# Revit family: Hager-Golf-IP40-Plain_Door-sistema-PT-pt
name_source: partatom
category: Electrical Equipment
units: mm (PartAtom-declared; Revit-internal decimal feet)

## family parameters
Cut with Voids When Loaded = No
Host = Face
Panel Configuration = Two Columns, Circuits Across
Part Type = Panelboard
Room Calculation Point = No
Round Connector Dimension = Use Diameter
Shared = No

## types (31) — shared parameters
EF000007 - Cor = EV000202 - Branco
EF000116 - Número RAL = 9010
EF000118 - Com tampa de montagem = No
EF000339 - Tipo de difusor = EV004216 - Porta
EF001062 - Versão EMC = No
EF001088 - Extensão possível = Yes
EF001134 - Calha DIN = Yes
EF001596 - Material do corpo = EV000139 - Plástico
EF004462 - Tipo de fecho = EV000154 - Outro
EF006244 - Tampa/porta transparente = No
EF006306 - Com fecho = No
EF009212 - Tipo de tampa = EV000116 - Fechado
EF015776 - Borne de terra = Yes
EF015941 - Porta para passagem de sinal = Yes
HG000001 - Número de colunas = 1
HG000002 - Com porta ou tampa = Yes
HG000003 - Gama = Golf
HG000005 - Espessura = 3 mm  [stored 0.00984252 ft]
HG000009 - Porta dupla = No
HG000010 - Portas assimétricas = No
HG000011 - Filas vazias desde da parte de baixo = No
HG000017 - Distância entre polos = 18 mm  [stored 0.0590551 ft]
Manufacturer = Hager
Type Comments = Golf
zero-valued in all types: Default Elevation, HG000007 - Número de colunas vazias, HG000008 - Número de filas vazias

## per-type parameters (varying)
| type | EF000003 - Método de montagem | EF000008 - Largura | EF000040 - Altura | EF000049 - Profundidade | EF000218 - Profundidade incorporada | EF000266 - Número de linhas | EF000332 - Altura embutida | EF000846 - Largura para embutir | EF001131 - Profundidade interior | EF002950 - Largura em número de módulos | EF005474 - Grau de proteção (IP) | EF015777 - Borne de neutro | HG000004 - Referência do Fabricante | HG000006 - Encastrado | Model |
| Montagem em superfície  L138 A184 P99 4 unidade de divisão - VS104PP | EV000384 - Montagem em superfície (gesso) | 138 mm  [stored 0.452756 ft] | 184 mm  [stored 0.603675 ft] | 99 mm  [stored 0.324803 ft] | 0 mm  [stored 0 ft] | 1 | 0 mm  [stored 0 ft] | 0 mm  [stored 0 ft] | 99 mm  [stored 0.324803 ft] | 4 |  | Yes | VS104PP | No | VS104PP |
| Montagem em superfície  L210 A184 P99 8 unidade de divisão - VS108PP | EV000384 - Montagem em superfície (gesso) | 210 mm  [stored 0.688976 ft] | 184 mm  [stored 0.603675 ft] | 99 mm  [stored 0.324803 ft] | 0 mm  [stored 0 ft] | 1 | 0 mm  [stored 0 ft] | 0 mm  [stored 0 ft] | 99 mm  [stored 0.324803 ft] | 8 |  | Yes | VS108PP | No | VS108PP |
| Montagem em superfície IP40 L282 A252 P99 12 unidade de divisão - VS112PP | EV000384 - Montagem em superfície (gesso) | 282 mm | 252 mm  [stored 0.826772 ft] | 99 mm  [stored 0.324803 ft] | 0 mm  [stored 0 ft] | 1 | 0 mm  [stored 0 ft] | 0 mm  [stored 0 ft] | 99 mm  [stored 0.324803 ft] | 12 | EV006415 - IP40 | Yes | VS112PP | No | VS112PP |
| Montagem em superfície IP40 L282 A377 P99 12 unidade de divisão - VS212PP | EV000384 - Montagem em superfície (gesso) | 282 mm | 377 mm  [stored 1.23688 ft] | 99 mm  [stored 0.324803 ft] | 0 mm  [stored 0 ft] | 2 | 0 mm  [stored 0 ft] | 0 mm  [stored 0 ft] | 99 mm  [stored 0.324803 ft] | 12 | EV006415 - IP40 | Yes | VS212PP | No | VS212PP |
| Montagem em superfície IP40 L282 A500 P99 12 unidade de divisão - VS312PP | EV000384 - Montagem em superfície (gesso) | 282 mm | 500 mm  [stored 1.64042 ft] | 99 mm  [stored 0.324803 ft] | 0 mm  [stored 0 ft] | 3 | 0 mm  [stored 0 ft] | 0 mm  [stored 0 ft] | 99 mm  [stored 0.324803 ft] | 12 | EV006415 - IP40 | Yes | VS312PP | No | VS312PP |
| Montagem em superfície IP40 L282 A647 P99 12 unidade de divisão - VS412PP | EV000384 - Montagem em superfície (gesso) | 282 mm | 647 mm  [stored 2.1227 ft] | 99 mm  [stored 0.324803 ft] | 0 mm  [stored 0 ft] | 4 | 0 mm  [stored 0 ft] | 0 mm  [stored 0 ft] | 99 mm  [stored 0.324803 ft] | 12 | EV006415 - IP40 | Yes | VS412PP | No | VS412PP |
| Montagem em superfície IP40 L390 A252 P99 18 unidade de divisão - VS118PP | EV000384 - Montagem em superfície (gesso) | 390 mm  [stored 1.27953 ft] | 252 mm  [stored 0.826772 ft] | 99 mm  [stored 0.324803 ft] | 0 mm  [stored 0 ft] | 1 | 0 mm  [stored 0 ft] | 0 mm  [stored 0 ft] | 99 mm  [stored 0.324803 ft] | 18 | EV006415 - IP40 | Yes | VS118PP | No | VS118PP |
| Montagem em superfície IP40 L390 A377 P99 18 unidade de divisão - VS218PP | EV000384 - Montagem em superfície (gesso) | 390 mm  [stored 1.27953 ft] | 377 mm  [stored 1.23688 ft] | 99 mm  [stored 0.324803 ft] | 0 mm  [stored 0 ft] | 2 | 0 mm  [stored 0 ft] | 0 mm  [stored 0 ft] | 99 mm  [stored 0.324803 ft] | 18 | EV006415 - IP40 | Yes | VS218PP | No | VS218PP |
| Montagem em superfície IP40 L390 A500 P99 18 unidade de divisão - VS318PP | EV000384 - Montagem em superfície (gesso) | 390 mm  [stored 1.27953 ft] | 500 mm  [stored 1.64042 ft] | 99 mm  [stored 0.324803 ft] | 0 mm  [stored 0 ft] | 3 | 0 mm  [stored 0 ft] | 0 mm  [stored 0 ft] | 99 mm  [stored 0.324803 ft] | 18 | EV006415 - IP40 | Yes | VS318PP | No | VS318PP |
| Montagem em superfície IP40 L390 A647 P99 18 unidade de divisão - VS418PP | EV000384 - Montagem em superfície (gesso) | 390 mm  [stored 1.27953 ft] | 647 mm  [stored 2.1227 ft] | 99 mm  [stored 0.324803 ft] | 0 mm  [stored 0 ft] | 4 | 0 mm  [stored 0 ft] | 0 mm  [stored 0 ft] | 99 mm  [stored 0.324803 ft] | 18 | EV006415 - IP40 | Yes | VS418PP | No | VS418PP |
| Montagem em superfície IP40 L462 A252 P99 22 unidade de divisão - VS122PP | EV000384 - Montagem em superfície (gesso) | 462 mm  [stored 1.51575 ft] | 252 mm  [stored 0.826772 ft] | 99 mm  [stored 0.324803 ft] | 0 mm  [stored 0 ft] | 1 | 0 mm  [stored 0 ft] | 0 mm  [stored 0 ft] | 99 mm  [stored 0.324803 ft] | 22 | EV006415 - IP40 | Yes | VS122PP | No | VS122PP |
| Montagem embutida  L204 A225 P97.5 4 unidade de divisão - VF104PP | EV000383 - Montagem embutida (gesso) | 204 mm | 225 mm  [stored 0.738189 ft] | 98 mm  [stored 0.321522 ft] | 72 mm  [stored 0.23622 ft] | 1 | 189 mm  [stored 0.620079 ft] | 170 mm  [stored 0.557743 ft] | 98 mm  [stored 0.321522 ft] | 4 |  | Yes | VF104PP | Yes | VF104PP |
| Montagem embutida  L275 A225 P97.5 8 unidade de divisão - VF108PEH | EV000383 - Montagem embutida (gesso) | 275 mm | 225 mm  [stored 0.738189 ft] | 98 mm  [stored 0.321522 ft] | 72 mm  [stored 0.23622 ft] | 1 | 189 mm  [stored 0.620079 ft] | 242 mm  [stored 0.793963 ft] | 98 mm  [stored 0.321522 ft] | 8 |  | No | VF108PEH | Yes | VF108PEH |
| Montagem embutida  L275 A225 P97.5 8 unidade de divisão - VF108PP | EV000383 - Montagem embutida (gesso) | 275 mm | 225 mm  [stored 0.738189 ft] | 98 mm  [stored 0.321522 ft] | 72 mm  [stored 0.23622 ft] | 1 | 189 mm  [stored 0.620079 ft] | 242 mm  [stored 0.793963 ft] | 98 mm  [stored 0.321522 ft] | 8 |  | Yes | VF108PP | Yes | VF108PP |
| Montagem embutida IP40 L352 A293 P97.5 12 unidade de divisão - VF112PEH | EV000383 - Montagem embutida (gesso) | 352 mm  [stored 1.15486 ft] | 293 mm | 98 mm  [stored 0.321522 ft] | 72 mm  [stored 0.23622 ft] | 1 | 257 mm  [stored 0.843176 ft] | 318 mm  [stored 1.04331 ft] | 98 mm  [stored 0.321522 ft] | 12 | EV006415 - IP40 | No | VF112PEH | Yes | VF112PEH |
| Montagem embutida IP40 L352 A293 P97.5 12 unidade de divisão - VF112PP | EV000383 - Montagem embutida (gesso) | 352 mm  [stored 1.15486 ft] | 293 mm | 98 mm  [stored 0.321522 ft] | 72 mm  [stored 0.23622 ft] | 1 | 257 mm  [stored 0.843176 ft] | 318 mm  [stored 1.04331 ft] | 98 mm  [stored 0.321522 ft] | 12 | EV006415 - IP40 | Yes | VF112PP | Yes | VF112PP |
| Montagem embutida IP40 L352 A543 P97.5 12 unidade de divisão - VF312PEH | EV000383 - Montagem embutida (gesso) | 352 mm  [stored 1.15486 ft] | 543 mm  [stored 1.7815 ft] | 98 mm  [stored 0.321522 ft] | 72 mm  [stored 0.23622 ft] | 3 | 507 mm  [stored 1.66339 ft] | 318 mm  [stored 1.04331 ft] | 98 mm  [stored 0.321522 ft] | 12 | EV006415 - IP40 | No | VF312PEH | Yes | VF312PEH |
| Montagem embutida IP40 L352 A543 P97.5 12 unidade de divisão - VF312PP | EV000383 - Montagem embutida (gesso) | 352 mm  [stored 1.15486 ft] | 543 mm  [stored 1.7815 ft] | 98 mm  [stored 0.321522 ft] | 72 mm  [stored 0.23622 ft] | 3 | 507 mm  [stored 1.66339 ft] | 318 mm  [stored 1.04331 ft] | 98 mm  [stored 0.321522 ft] | 12 | EV006415 - IP40 | Yes | VF312PP | Yes | VF312PP |
| Montagem embutida IP40 L352 A688 P97.5 12 unidade de divisão - VF412PEH | EV000383 - Montagem embutida (gesso) | 352 mm  [stored 1.15486 ft] | 688 mm  [stored 2.25722 ft] | 98 mm  [stored 0.321522 ft] | 72 mm  [stored 0.23622 ft] | 4 | 652 mm  [stored 2.13911 ft] | 318 mm  [stored 1.04331 ft] | 98 mm  [stored 0.321522 ft] | 12 | EV006415 - IP40 | No | VF412PEH | Yes | VF412PEH |
| Montagem embutida IP40 L352 A688 P97.5 12 unidade de divisão - VF412PP | EV000383 - Montagem embutida (gesso) | 352 mm  [stored 1.15486 ft] | 688 mm  [stored 2.25722 ft] | 98 mm  [stored 0.321522 ft] | 72 mm  [stored 0.23622 ft] | 4 | 652 mm  [stored 2.13911 ft] | 318 mm  [stored 1.04331 ft] | 98 mm  [stored 0.321522 ft] | 12 | EV006415 - IP40 | Yes | VF412PP | Yes | VF412PP |
| Montagem embutida IP40 L382 A418 P97.5 12 unidade de divisão - VF212PEH | EV000383 - Montagem embutida (gesso) | 382 mm  [stored 1.25328 ft] | 418 mm  [stored 1.37139 ft] | 98 mm  [stored 0.321522 ft] | 72 mm  [stored 0.23622 ft] | 2 | 382 mm  [stored 1.25328 ft] | 318 mm  [stored 1.04331 ft] | 98 mm  [stored 0.321522 ft] | 12 | EV006415 - IP40 | No | VF212PEH | Yes | VF212PEH |
| Montagem embutida IP40 L382 A418 P97.5 12 unidade de divisão - VF212PP | EV000383 - Montagem embutida (gesso) | 382 mm  [stored 1.25328 ft] | 418 mm  [stored 1.37139 ft] | 98 mm  [stored 0.321522 ft] | 72 mm  [stored 0.23622 ft] | 2 | 382 mm  [stored 1.25328 ft] | 318 mm  [stored 1.04331 ft] | 98 mm  [stored 0.321522 ft] | 12 | EV006415 - IP40 | Yes | VF212PP | Yes | VF212PP |
| Montagem embutida IP40 L460 A293 P97.5 18 unidade de divisão - VF118PEH | EV000383 - Montagem embutida (gesso) | 460 mm  [stored 1.50919 ft] | 293 mm | 98 mm  [stored 0.321522 ft] | 72 mm  [stored 0.23622 ft] | 1 | 257 mm  [stored 0.843176 ft] | 426 mm  [stored 1.39764 ft] | 98 mm  [stored 0.321522 ft] | 18 | EV006415 - IP40 | No | VF118PEH | Yes | VF118PEH |
| Montagem embutida IP40 L460 A293 P97.5 18 unidade de divisão - VF118PP | EV000383 - Montagem embutida (gesso) | 460 mm  [stored 1.50919 ft] | 293 mm | 98 mm  [stored 0.321522 ft] | 72 mm  [stored 0.23622 ft] | 1 | 257 mm  [stored 0.843176 ft] | 426 mm  [stored 1.39764 ft] | 98 mm  [stored 0.321522 ft] | 18 | EV006415 - IP40 | Yes | VF118PP | Yes | VF118PP |
| Montagem embutida IP40 L460 A418 P97.5 18 unidade de divisão - VF218PEH | EV000383 - Montagem embutida (gesso) | 460 mm  [stored 1.50919 ft] | 418 mm  [stored 1.37139 ft] | 98 mm  [stored 0.321522 ft] | 72 mm  [stored 0.23622 ft] | 2 | 382 mm  [stored 1.25328 ft] | 426 mm  [stored 1.39764 ft] | 98 mm  [stored 0.321522 ft] | 18 | EV006415 - IP40 | No | VF218PEH | Yes | VF218PEH |
| Montagem embutida IP40 L460 A418 P97.5 18 unidade de divisão - VF218PP | EV000383 - Montagem embutida (gesso) | 460 mm  [stored 1.50919 ft] | 418 mm  [stored 1.37139 ft] | 98 mm  [stored 0.321522 ft] | 72 mm  [stored 0.23622 ft] | 2 | 382 mm  [stored 1.25328 ft] | 426 mm  [stored 1.39764 ft] | 98 mm  [stored 0.321522 ft] | 18 | EV006415 - IP40 | Yes | VF218PP | Yes | VF218PP |
| Montagem embutida IP40 L460 A543 P97.5 18 unidade de divisão - VF318PEH | EV000383 - Montagem embutida (gesso) | 460 mm  [stored 1.50919 ft] | 543 mm  [stored 1.7815 ft] | 98 mm  [stored 0.321522 ft] | 72 mm  [stored 0.23622 ft] | 3 | 507 mm  [stored 1.66339 ft] | 426 mm  [stored 1.39764 ft] | 98 mm  [stored 0.321522 ft] | 18 | EV006415 - IP40 | No | VF318PEH | Yes | VF318PEH |
| Montagem embutida IP40 L460 A543 P97.5 18 unidade de divisão - VF318PP | EV000383 - Montagem embutida (gesso) | 460 mm  [stored 1.50919 ft] | 543 mm  [stored 1.7815 ft] | 98 mm  [stored 0.321522 ft] | 72 mm  [stored 0.23622 ft] | 3 | 507 mm  [stored 1.66339 ft] | 426 mm  [stored 1.39764 ft] | 98 mm  [stored 0.321522 ft] | 18 | EV006415 - IP40 | Yes | VF318PP | Yes | VF318PP |
| Montagem embutida IP40 L460 A688 P97.5 18 unidade de divisão - VF418PEH | EV000383 - Montagem embutida (gesso) | 460 mm  [stored 1.50919 ft] | 688 mm  [stored 2.25722 ft] | 98 mm  [stored 0.321522 ft] | 72 mm  [stored 0.23622 ft] | 4 | 652 mm  [stored 2.13911 ft] | 426 mm  [stored 1.39764 ft] | 98 mm  [stored 0.321522 ft] | 18 | EV006415 - IP40 | No | VF418PEH | Yes | VF418PEH |
| Montagem embutida IP40 L460 A688 P97.5 18 unidade de divisão - VF418PP | EV000383 - Montagem embutida (gesso) | 460 mm  [stored 1.50919 ft] | 688 mm  [stored 2.25722 ft] | 98 mm  [stored 0.321522 ft] | 72 mm  [stored 0.23622 ft] | 4 | 652 mm  [stored 2.13911 ft] | 426 mm  [stored 1.39764 ft] | 98 mm  [stored 0.321522 ft] | 18 | EV006415 - IP40 | Yes | VF418PP | Yes | VF418PP |
| Montagem embutida IP40 L532 A293 P97.5 22 unidade de divisão - VF122PP | EV000383 - Montagem embutida (gesso) | 532 mm  [stored 1.74541 ft] | 293 mm | 98 mm  [stored 0.321522 ft] | 72 mm  [stored 0.23622 ft] | 1 | 257 mm  [stored 0.843176 ft] | 498 mm  [stored 1.63386 ft] | 98 mm  [stored 0.321522 ft] | 22 | EV006415 - IP40 | Yes | VF122PP | Yes | VF122PP |

note: [stored X ft] marks values corroborated as IEEE doubles in the binary element streams (Revit-internal decimal feet)

## geometry (parser evidence)
native form markers: Sweep x17
no freeform markers — native parametric forms only
